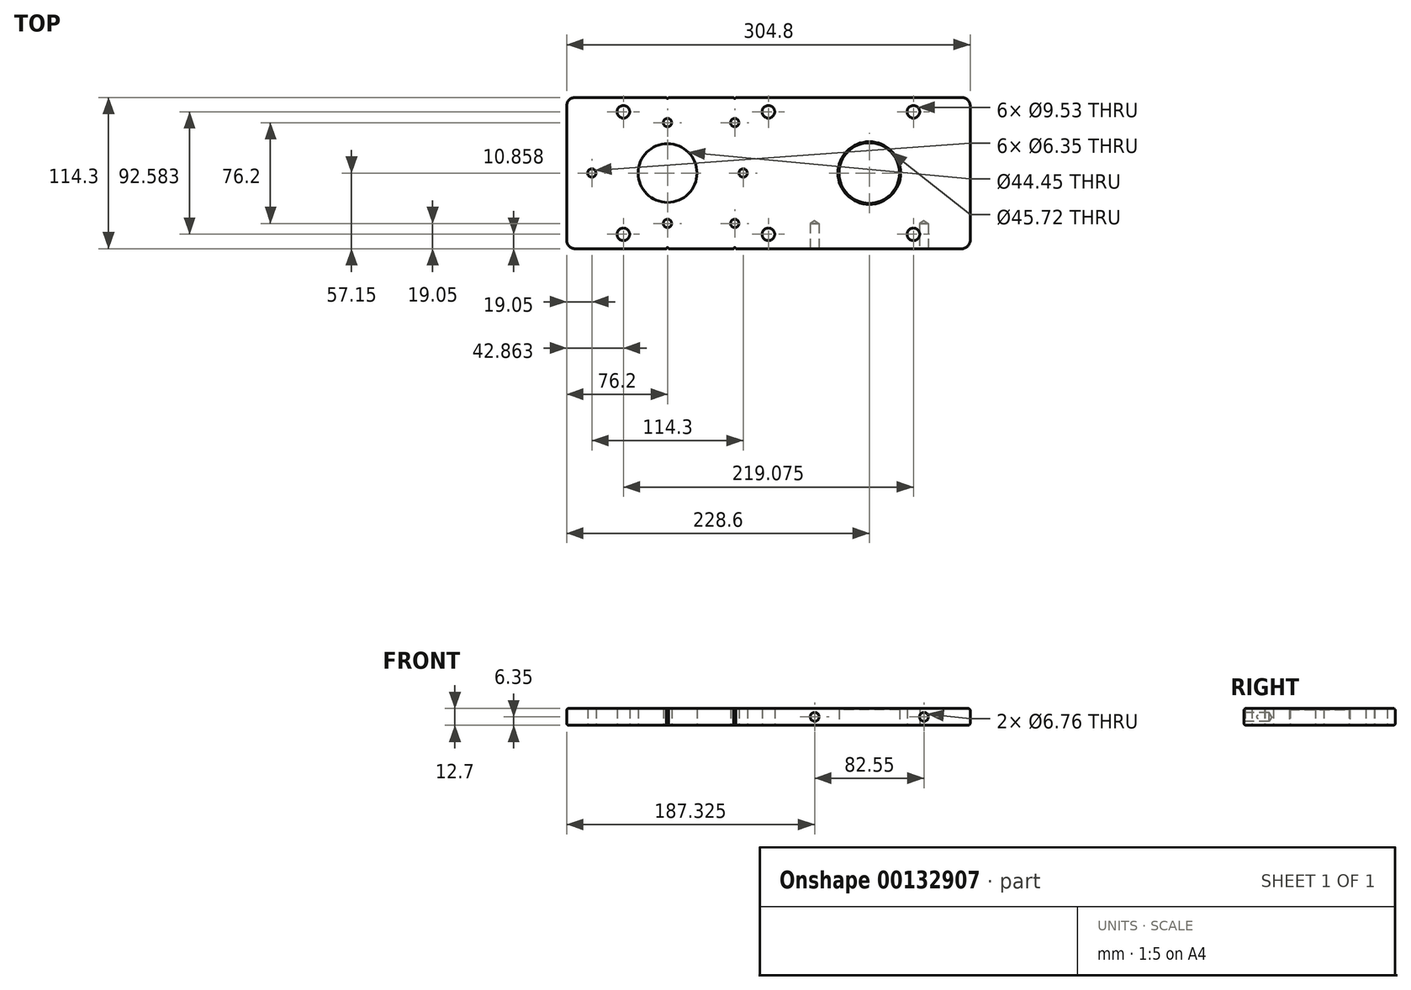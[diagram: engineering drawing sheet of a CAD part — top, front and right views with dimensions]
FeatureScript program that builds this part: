
annotation { "Feature Type Name" : "Feature", "Feature Type Description" : "" }
export const myFeature = defineFeature(function(context is Context, id is Id, definition is map)
    precondition{}
    {
        {
            var Q0;
            Q0=qCreatedBy(makeId("Top.planeOp"),FACE);
            var sketch = newSketch(context, id + "F0", { "sketchPlane" : qUnion([Q0])});
            skLineSegment(sketch, "E0.bottom", {"start": v(152.4, 57.15) * mm, "end": v(-24.61, 57.15) * mm});
            skLineSegment(sketch, "E0.top", {"start": v(152.4, -57.15) * mm, "end": v(-24.61, -57.15) * mm});
            skLineSegment(sketch, "E0.left", {"start": v(152.4, 57.15) * mm, "end": v(152.4, -57.15) * mm});
            skLineSegment(sketch, "E0.right", {"start": v(-152.4, 57.15) * mm, "end": v(-152.4, -57.15) * mm});
            skPoint(sketch, "E0.middle", {"position": v(0, 0) * mm});
            skLineSegment(sketch, "E1", {"start": v(-152.4, 0) * mm, "end": v(152.4, 0) * mm, "construction": true});
            skLineSegment(sketch, "E2", {"start": v(0, 57.15) * mm, "end": v(0, -57.15) * mm, "construction": true});
            skCircle(sketch, "E3", {"center": v(-109.54, 46.3) * mm, "radius": 4.76 * mm});
            skCircle(sketch, "E4.MirrorC", {"center": v(-109.54, -46.3) * mm, "radius": 4.76 * mm});
            skLineSegment(sketch, "E5.MirrorCS", {"start": v(0, -57.15) * mm, "end": v(0, 57.15) * mm, "construction": true});
            skCircle(sketch, "E6.MirrorC", {"center": v(109.54, 46.3) * mm, "radius": 4.76 * mm});
            skCircle(sketch, "E7.MirrorC", {"center": v(109.54, -46.3) * mm, "radius": 4.76 * mm});
            skCircle(sketch, "E8", {"center": v(-76.2, 0) * mm, "radius": 22.23 * mm});
            skCircle(sketch, "E9", {"center": v(76.2, 0) * mm, "radius": 22.86 * mm});
            skArc(sketch, "E10", {"start": v(-76.99, 57.15) * mm, "mid": v(-76.2, 56.36) * mm, "end": v(-75.41, 57.15) * mm});
            skArc(sketch, "E11.MirrorC", {"start": v(-76.99, -57.15) * mm, "mid": v(-76.2, -56.36) * mm, "end": v(-75.41, -57.15) * mm});
            skLineSegment(sketch, "E12.trimOffspring", {"start": v(-76.99, 57.15) * mm, "end": v(-152.4, 57.15) * mm});
            skLineSegment(sketch, "E13.trimOffspring", {"start": v(-76.99, -57.15) * mm, "end": v(-152.4, -57.15) * mm});
            skArc(sketch, "E14.1.0.0", {"start": v(-26.19, -57.15) * mm, "mid": v(-25.4, -56.36) * mm, "end": v(-24.61, -57.15) * mm});
            skArc(sketch, "E14.1.0.1", {"start": v(-26.19, 57.15) * mm, "mid": v(-25.4, 56.36) * mm, "end": v(-24.61, 57.15) * mm});
            skLineSegment(sketch, "E14.direction1", {"start": v(-76.99, -57.15) * mm, "end": v(-26.19, -57.15) * mm, "construction": true});
            skLineSegment(sketch, "E15.trimOffspring", {"start": v(-26.19, 57.15) * mm, "end": v(-75.41, 57.15) * mm});
            skLineSegment(sketch, "E16.trimOffspring", {"start": v(-26.19, -57.15) * mm, "end": v(-75.41, -57.15) * mm});
            skCircle(sketch, "E17", {"center": v(-133.35, 0) * mm, "radius": 3.18 * mm});
            skCircle(sketch, "E18", {"center": v(-19.05, 0) * mm, "radius": 3.18 * mm});
            skCircle(sketch, "E19", {"center": v(0, -46.3) * mm, "radius": 4.76 * mm});
            skCircle(sketch, "E20", {"center": v(0, 46.3) * mm, "radius": 4.76 * mm});
            skCircle(sketch, "E21", {"center": v(-25.4, -38.1) * mm, "radius": 3.18 * mm});
            skCircle(sketch, "E22", {"center": v(-76.2, -38.1) * mm, "radius": 3.18 * mm});
            skCircle(sketch, "E23.MirrorC", {"center": v(-76.2, 38.1) * mm, "radius": 3.18 * mm});
            skCircle(sketch, "E24.MirrorC", {"center": v(-25.4, 38.1) * mm, "radius": 3.18 * mm});
            skSolve(sketch);
        }
        {
            var Q0;
            Q0=makeQuery(id+"F0.imprint","IMPRINT",FACE,{"disambiguationData":[TD([[makeQuery(id+"F0.imprint","IMPRINT",EDGE,{"derivedFrom":sQuery(id+"F0.wireOp",EDGE,"E0.bottom")}),1.0]])]});
            extrude(context, id + "F1", {"entities" : qUnion([Q0]), "endBound" : BoundingType.SYMMETRIC, "depth" : 12.7 * mm});
        }
        {
            var Q0;
            Q0=makeQuery(id+"F1.opExtrude","SWEPT_EDGE",EDGE,{"disambiguationData":[OSD([sQuery(id+"F0.wireOp",EDGE,"E0.right"),sQuery(id+"F0.wireOp",EDGE,"E13.trimOffspring")])]});
            var Q1;
            Q1=makeQuery(id+"F1.opExtrude","SWEPT_EDGE",EDGE,{"disambiguationData":[OSD([sQuery(id+"F0.wireOp",EDGE,"E0.top"),sQuery(id+"F0.wireOp",EDGE,"E0.left")])]});
            var Q2;
            Q2=makeQuery(id+"F1.opExtrude","SWEPT_EDGE",EDGE,{"disambiguationData":[OSD([sQuery(id+"F0.wireOp",EDGE,"E0.bottom"),sQuery(id+"F0.wireOp",EDGE,"E0.left")])]});
            var Q3;
            Q3=makeQuery(id+"F1.opExtrude","SWEPT_EDGE",EDGE,{"disambiguationData":[OSD([sQuery(id+"F0.wireOp",EDGE,"E0.right"),sQuery(id+"F0.wireOp",EDGE,"E12.trimOffspring")])]});
            fillet(context, id + "F2", {"entities" : qUnion([Q0, Q1, Q2, Q3]), "radius" : 6.35 * mm, "tangentPropagation" : true, "allowEdgeOverflow" : false});
        }
        {
            var Q0;
            Q0=makeQuery(id+"F1.opExtrude","CAP_EDGE",EDGE,{"disambiguationData":[OSD([sQuery(id+"F0.wireOp",EDGE,"E0.bottom")])],"isStart":false});
            var Q1;
            Q1=makeQuery(id+"F1.opExtrude","CAP_EDGE",EDGE,{"disambiguationData":[OSD([sQuery(id+"F0.wireOp",EDGE,"E0.bottom")])],"isStart":true});
            var Q2;
            {var subQ0=sQuery(id+"F0.wireOp",EDGE,"E12.trimOffspring");var subQ1=sQuery(id+"F0.wireOp",EDGE,"E0.right");Q2=makeQuery(id+"F2.opFillet","BLEND_EDGE",EDGE,{"blendedFrom":[makeQuery(id+"F1.opExtrude","SWEPT_EDGE",EDGE,{"disambiguationData":[OSD([subQ1,subQ0])]}),makeQuery(id+"F1.opExtrude","CAP_FACE",FACE,{"disambiguationData":[OSD([sQuery(id+"F0.wireOp",EDGE,"E0.bottom"),sQuery(id+"F0.wireOp",EDGE,"E0.top"),sQuery(id+"F0.wireOp",EDGE,"E0.left"),subQ1,sQuery(id+"F0.wireOp",EDGE,"E3"),sQuery(id+"F0.wireOp",EDGE,"E4.MirrorC"),sQuery(id+"F0.wireOp",EDGE,"E6.MirrorC"),sQuery(id+"F0.wireOp",EDGE,"E7.MirrorC"),sQuery(id+"F0.wireOp",EDGE,"E8"),sQuery(id+"F0.wireOp",EDGE,"E9"),sQuery(id+"F0.wireOp",EDGE,"E10"),sQuery(id+"F0.wireOp",EDGE,"E11.MirrorC"),subQ0,sQuery(id+"F0.wireOp",EDGE,"E13.trimOffspring"),sQuery(id+"F0.wireOp",EDGE,"E14.1.0.0"),sQuery(id+"F0.wireOp",EDGE,"E14.1.0.1"),sQuery(id+"F0.wireOp",EDGE,"E15.trimOffspring"),sQuery(id+"F0.wireOp",EDGE,"E16.trimOffspring"),sQuery(id+"F0.wireOp",EDGE,"E17"),sQuery(id+"F0.wireOp",EDGE,"E18")])],"isStart":false})],"blendedInto":[makeQuery(id+"F1.opExtrude","CAP_FACE",FACE,{"disambiguationData":[OSD([sQuery(id+"F0.wireOp",EDGE,"E0.bottom"),sQuery(id+"F0.wireOp",EDGE,"E0.top"),sQuery(id+"F0.wireOp",EDGE,"E0.left"),subQ1,sQuery(id+"F0.wireOp",EDGE,"E3"),sQuery(id+"F0.wireOp",EDGE,"E4.MirrorC"),sQuery(id+"F0.wireOp",EDGE,"E6.MirrorC"),sQuery(id+"F0.wireOp",EDGE,"E7.MirrorC"),sQuery(id+"F0.wireOp",EDGE,"E8"),sQuery(id+"F0.wireOp",EDGE,"E9"),sQuery(id+"F0.wireOp",EDGE,"E10"),sQuery(id+"F0.wireOp",EDGE,"E11.MirrorC"),subQ0,sQuery(id+"F0.wireOp",EDGE,"E13.trimOffspring"),sQuery(id+"F0.wireOp",EDGE,"E14.1.0.0"),sQuery(id+"F0.wireOp",EDGE,"E14.1.0.1"),sQuery(id+"F0.wireOp",EDGE,"E15.trimOffspring"),sQuery(id+"F0.wireOp",EDGE,"E16.trimOffspring"),sQuery(id+"F0.wireOp",EDGE,"E17"),sQuery(id+"F0.wireOp",EDGE,"E18")])],"isStart":false})]});}
            var Q3;
            Q3=makeQuery(id+"F1.opExtrude","CAP_EDGE",EDGE,{"disambiguationData":[OSD([sQuery(id+"F0.wireOp",EDGE,"E0.right")])],"isStart":false});
            var Q4;
            {var subQ0=sQuery(id+"F0.wireOp",EDGE,"E12.trimOffspring");var subQ1=sQuery(id+"F0.wireOp",EDGE,"E0.right");Q4=makeQuery(id+"F2.opFillet","BLEND_EDGE",EDGE,{"blendedFrom":[makeQuery(id+"F1.opExtrude","SWEPT_EDGE",EDGE,{"disambiguationData":[OSD([subQ1,subQ0])]}),makeQuery(id+"F1.opExtrude","CAP_FACE",FACE,{"disambiguationData":[OSD([sQuery(id+"F0.wireOp",EDGE,"E0.bottom"),sQuery(id+"F0.wireOp",EDGE,"E0.top"),sQuery(id+"F0.wireOp",EDGE,"E0.left"),subQ1,sQuery(id+"F0.wireOp",EDGE,"E3"),sQuery(id+"F0.wireOp",EDGE,"E4.MirrorC"),sQuery(id+"F0.wireOp",EDGE,"E6.MirrorC"),sQuery(id+"F0.wireOp",EDGE,"E7.MirrorC"),sQuery(id+"F0.wireOp",EDGE,"E8"),sQuery(id+"F0.wireOp",EDGE,"E9"),sQuery(id+"F0.wireOp",EDGE,"E10"),sQuery(id+"F0.wireOp",EDGE,"E11.MirrorC"),subQ0,sQuery(id+"F0.wireOp",EDGE,"E13.trimOffspring"),sQuery(id+"F0.wireOp",EDGE,"E14.1.0.0"),sQuery(id+"F0.wireOp",EDGE,"E14.1.0.1"),sQuery(id+"F0.wireOp",EDGE,"E15.trimOffspring"),sQuery(id+"F0.wireOp",EDGE,"E16.trimOffspring"),sQuery(id+"F0.wireOp",EDGE,"E17"),sQuery(id+"F0.wireOp",EDGE,"E18")])],"isStart":true})],"blendedInto":[makeQuery(id+"F1.opExtrude","CAP_FACE",FACE,{"disambiguationData":[OSD([sQuery(id+"F0.wireOp",EDGE,"E0.bottom"),sQuery(id+"F0.wireOp",EDGE,"E0.top"),sQuery(id+"F0.wireOp",EDGE,"E0.left"),subQ1,sQuery(id+"F0.wireOp",EDGE,"E3"),sQuery(id+"F0.wireOp",EDGE,"E4.MirrorC"),sQuery(id+"F0.wireOp",EDGE,"E6.MirrorC"),sQuery(id+"F0.wireOp",EDGE,"E7.MirrorC"),sQuery(id+"F0.wireOp",EDGE,"E8"),sQuery(id+"F0.wireOp",EDGE,"E9"),sQuery(id+"F0.wireOp",EDGE,"E10"),sQuery(id+"F0.wireOp",EDGE,"E11.MirrorC"),subQ0,sQuery(id+"F0.wireOp",EDGE,"E13.trimOffspring"),sQuery(id+"F0.wireOp",EDGE,"E14.1.0.0"),sQuery(id+"F0.wireOp",EDGE,"E14.1.0.1"),sQuery(id+"F0.wireOp",EDGE,"E15.trimOffspring"),sQuery(id+"F0.wireOp",EDGE,"E16.trimOffspring"),sQuery(id+"F0.wireOp",EDGE,"E17"),sQuery(id+"F0.wireOp",EDGE,"E18")])],"isStart":true})]});}
            fillet(context, id + "F3", {"entities" : qUnion([Q0, Q1, Q2, Q3, Q4]), "radius" : 1.57 * mm, "tangentPropagation" : true, "allowEdgeOverflow" : false});
        }
        {
            var Q0;
            Q0=makeQuery(id+"F1.opExtrude","CAP_EDGE",EDGE,{"disambiguationData":[OSD([sQuery(id+"F0.wireOp",EDGE,"E9")])],"isStart":false});
            chamfer(context, id + "F4", {"entities" : qUnion([Q0]), "width" : 0.81 * mm, "tangentPropagation" : true});
        }
        {
            var Q0;
            Q0=makeQuery(id+"F1.opExtrude","SWEPT_FACE",FACE,{"disambiguationData":[OSD([sQuery(id+"F0.wireOp",EDGE,"E0.top")])]});
            var sketch = newSketch(context, id + "F5", { "sketchPlane" : qUnion([Q0])});
            skPoint(sketch, "E25", {"position": v(34.93, 0) * mm});
            skPoint(sketch, "E26", {"position": v(117.48, 0) * mm});
            skSolve(sketch);
        }
        {
            var Q0;
            Q0=sQuery(id+"F5.wireOp",VERTEX,"E25");
            var Q1;
            Q1=sQuery(id+"F5.wireOp",VERTEX,"E26");
            var Q2;
            Q2=makeQuery(id+"F1.opExtrude","SWEPT_BODY",BODY,{"disambiguationData":[OSD([sQuery(id+"F0.wireOp",EDGE,"E0.bottom"),sQuery(id+"F0.wireOp",EDGE,"E0.top"),sQuery(id+"F0.wireOp",EDGE,"E0.left"),sQuery(id+"F0.wireOp",EDGE,"E0.right"),sQuery(id+"F0.wireOp",EDGE,"E3"),sQuery(id+"F0.wireOp",EDGE,"E4.MirrorC"),sQuery(id+"F0.wireOp",EDGE,"E6.MirrorC"),sQuery(id+"F0.wireOp",EDGE,"E7.MirrorC"),sQuery(id+"F0.wireOp",EDGE,"E8"),sQuery(id+"F0.wireOp",EDGE,"E9"),sQuery(id+"F0.wireOp",EDGE,"E10"),sQuery(id+"F0.wireOp",EDGE,"E11.MirrorC"),sQuery(id+"F0.wireOp",EDGE,"E12.trimOffspring"),sQuery(id+"F0.wireOp",EDGE,"E13.trimOffspring"),sQuery(id+"F0.wireOp",EDGE,"E14.1.0.0"),sQuery(id+"F0.wireOp",EDGE,"E14.1.0.1"),sQuery(id+"F0.wireOp",EDGE,"E15.trimOffspring"),sQuery(id+"F0.wireOp",EDGE,"E16.trimOffspring"),sQuery(id+"F0.wireOp",EDGE,"E17"),sQuery(id+"F0.wireOp",EDGE,"E18")])]});
            hole(context, id + "F6", {"style" : HoleStyle.SIMPLE, "endStyle" : HoleEndStyle.BLIND, "standardTappedOrClearance" : lookupTablePath({ "standard" : "ANSI", "fit" : "Normal (ASME)", "size" : "1/4", "type" : "Clearance" }), "standardBlindInLast" : lookupTablePath({ "fit" : "Free", "standard" : "ANSI", "size" : "1/4", "type" : "Clearance" }), "holeDiameter" : 6.76 * mm, "holeDepth" : 19.05 * mm, "locations" : qUnion([Q0, Q1]), "scope" : qUnion([Q2])});
        }
    });
